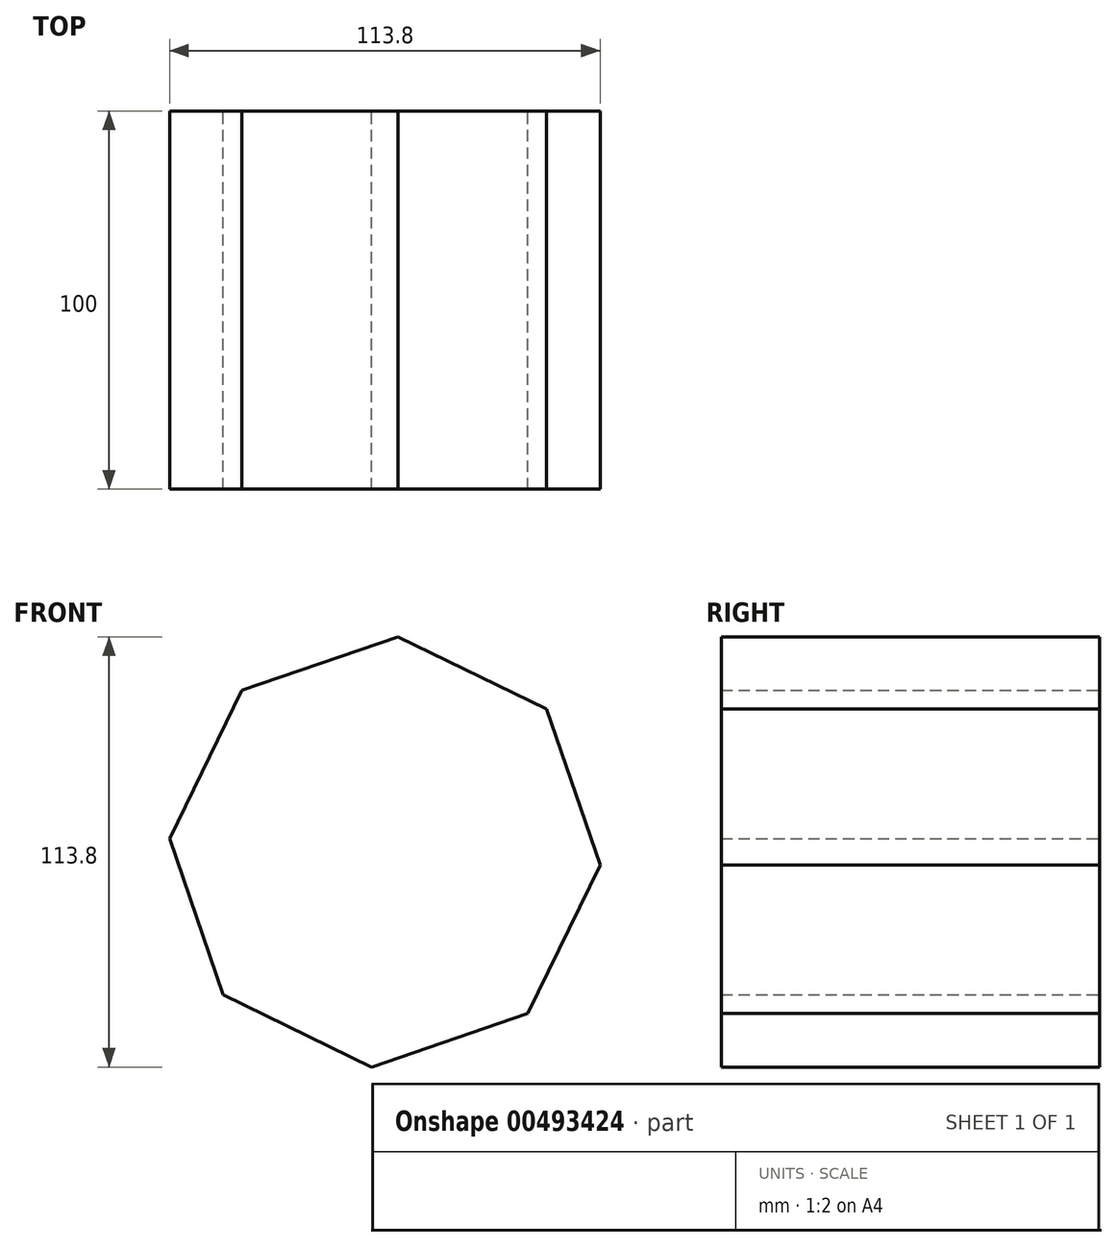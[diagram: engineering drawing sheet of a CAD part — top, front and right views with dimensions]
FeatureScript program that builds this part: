
annotation { "Feature Type Name" : "Feature", "Feature Type Description" : "" }
export const myFeature = defineFeature(function(context is Context, id is Id, definition is map)
    precondition{}
    {
        {
            var Q0;
            Q0=qCreatedBy(makeId("Front.planeOp"),FACE);
            var sketch = newSketch(context, id + "F0", { "sketchPlane" : qUnion([Q0])});
            skCircle(sketch, "E0.cCircle", {"center": v(0, 0) * mm, "radius": 57 * mm, "construction": true});
            skLineSegment(sketch, "E0.0", {"start": v(42.7, 37.77) * mm, "end": v(56.9, -3.5) * mm});
            skLineSegment(sketch, "E0.1", {"start": v(56.9, -3.5) * mm, "end": v(37.77, -42.7) * mm});
            skLineSegment(sketch, "E0.2", {"start": v(37.77, -42.7) * mm, "end": v(-3.5, -56.9) * mm});
            skLineSegment(sketch, "E0.3", {"start": v(-3.5, -56.9) * mm, "end": v(-42.7, -37.77) * mm});
            skLineSegment(sketch, "E0.4", {"start": v(-42.7, -37.77) * mm, "end": v(-56.9, 3.5) * mm});
            skLineSegment(sketch, "E0.5", {"start": v(-56.9, 3.5) * mm, "end": v(-37.77, 42.7) * mm});
            skLineSegment(sketch, "E0.6", {"start": v(-37.77, 42.7) * mm, "end": v(3.5, 56.9) * mm});
            skLineSegment(sketch, "E0.7", {"start": v(3.5, 56.9) * mm, "end": v(42.7, 37.77) * mm});
            skSolve(sketch);
        }
        {
            var Q0;
            Q0=makeQuery(id+"F0.imprint","IMPRINT",FACE,{"disambiguationData":[TD([[makeQuery(id+"F0.imprint","IMPRINT",EDGE,{"derivedFrom":sQuery(id+"F0.wireOp",EDGE,"E0.0")}),-1.0]])]});
            extrude(context, id + "F1", {"entities" : qUnion([Q0]), "depth" : 100 * mm});
        }
    });
